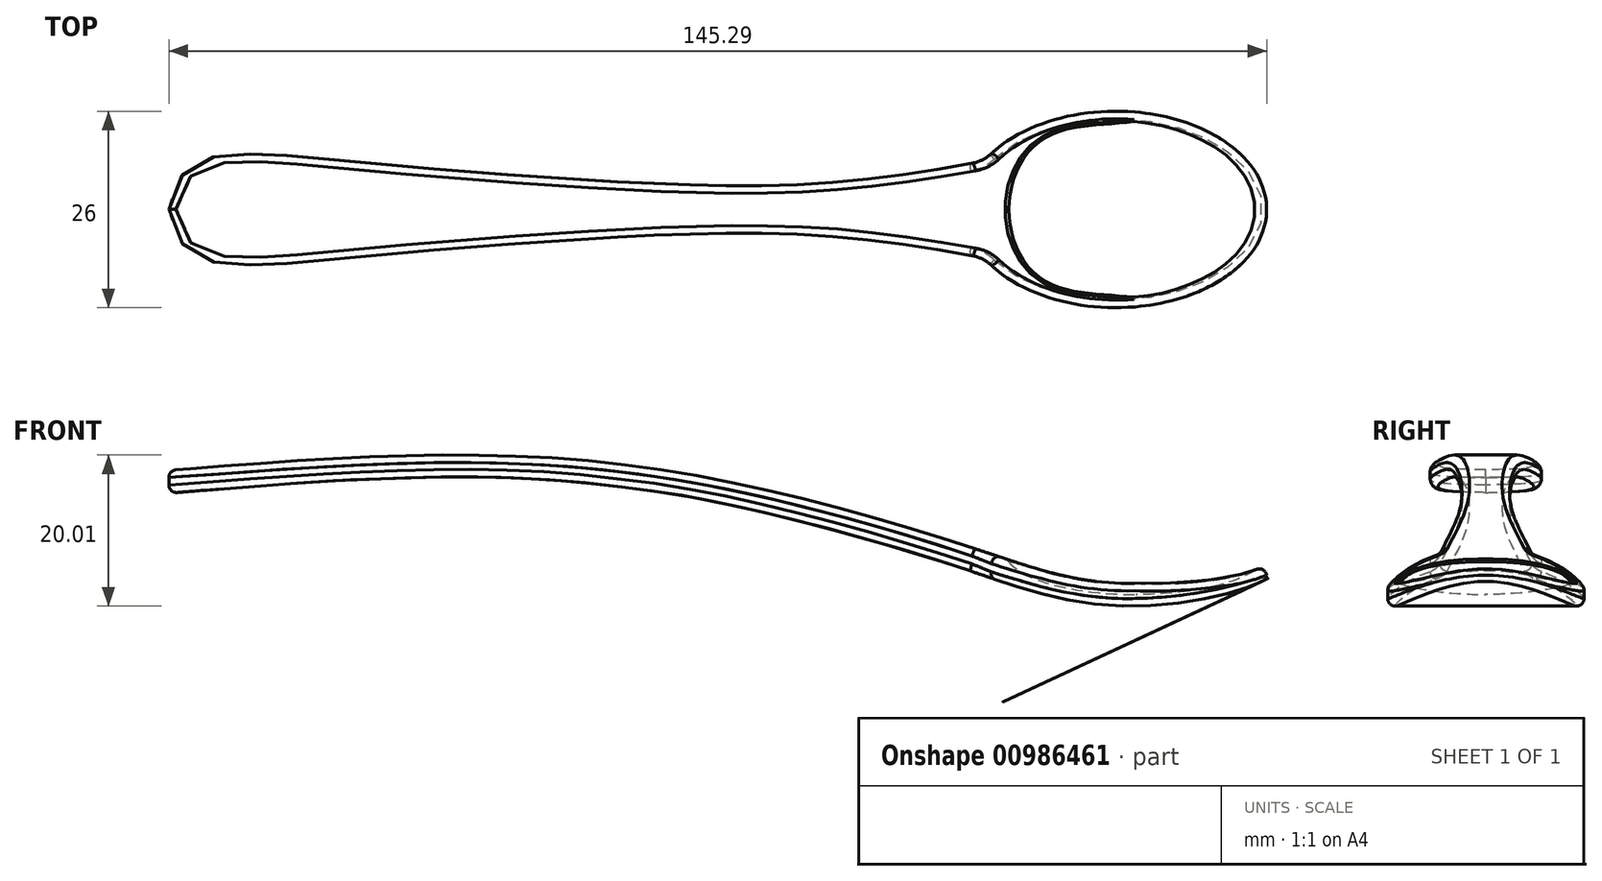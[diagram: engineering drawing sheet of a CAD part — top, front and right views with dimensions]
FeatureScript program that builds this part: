
annotation { "Feature Type Name" : "Feature", "Feature Type Description" : "" }
export const myFeature = defineFeature(function(context is Context, id is Id, definition is map)
    precondition{}
    {
        {
            var Q0;
            Q0=qCreatedBy(makeId("Top.planeOp"),FACE);
            var sketch = newSketch(context, id + "F0", { "sketchPlane" : qUnion([Q0])});
            skEllipticalArc(sketch, "E0", {});
            skFitSpline(sketch, "E1", {"points": [v(-17.42, 6.39) * mm, v(-40.4, 3.38) * mm, v(-73.2, 4.1) * mm, v(-102.87, 6.51) * mm, v(-120.96, 6.51) * mm, v(-124.34, 3.14) * mm, v(-125.3, 0) * mm], "startDerivative": vector(-109.7, -19.22) * mm, "endDerivative": vector(-9.68, -41.52) * mm});
            skLineSegment(sketch, "E2", {"start": v(-125.3, 0) * mm, "end": v(20, 0) * mm, "construction": true});
            skArc(sketch, "E3.filletArc", {"start": v(-19.02, 6.1) * mm, "mid": v(-17.64, 6.56) * mm, "end": v(-16.45, 7.4) * mm});
            skFitSpline(sketch, "E4.MirrorCS", {"points": [v(-17.42, -6.39) * mm, v(-40.4, -3.38) * mm, v(-73.2, -4.1) * mm, v(-102.87, -6.51) * mm, v(-120.96, -6.51) * mm, v(-124.34, -3.14) * mm, v(-125.3, 0) * mm], "startDerivative": vector(-109.7, 19.22) * mm, "endDerivative": vector(-9.68, 41.52) * mm});
            skEllipticalArc(sketch, "E5.MirrorCS", {});
            skArc(sketch, "E6.MirrorCS", {"start": v(-19.02, -6.1) * mm, "mid": v(-17.64, -6.56) * mm, "end": v(-16.45, -7.4) * mm});
            const initialGuessF0  = {"E0": [0, 0, 1, 0, 0.02, 0.013, 0, 2.5369205259482692], "E5.MirrorCS": [0, 0, 1, 0, 0.02, 0.013, 3.746264781231317, 0]};
            skSetInitialGuess(sketch, initialGuessF0);
            skSolve(sketch);
        }
        {
            var Q0;
            Q0=makeQuery(id+"F0.imprint","IMPRINT",FACE,{"disambiguationData":[TD([[makeQuery(id+"F0.imprint","IMPRINT",EDGE,{"derivedFrom":sQuery(id+"F0.wireOp",EDGE,"E0")}),1.0]])]});
            extrude(context, id + "F1", {"entities" : qUnion([Q0]), "depth" : 25 * mm, "offsetDistance" : 25 * mm});
        }
        {
            var Q0;
            Q0=qCreatedBy(makeId("Front.planeOp"),FACE);
            var sketch = newSketch(context, id + "F2", { "sketchPlane" : qUnion([Q0])});
            skLineSegment(sketch, "E7.0", {"start": v(-125.3, 25) * mm, "end": v(-125.3, 19.75) * mm});
            skLineSegment(sketch, "E8", {"start": v(20, 25) * mm, "end": v(20, 8.84) * mm});
            skFitSpline(sketch, "E9", {"points": [v(-125.3, 19.75) * mm, v(-92.2, 21.75) * mm, v(-59.48, 19.75) * mm, v(-29.68, 12.84) * mm, v(-15.87, 8.48) * mm, v(0, 4.85) * mm, v(16.12, 7.03) * mm, v(20, 8.84) * mm], "startDerivative": vector(178.78, 14.39) * mm, "endDerivative": vector(46, 26.97) * mm});
            skFitSpline(sketch, "E10.0", {"points": [v(-125.06, 16.76) * mm, v(-121.34, 17.06) * mm, v(-113.9, 17.66) * mm, v(-102.82, 18.4) * mm, v(-91.86, 18.83) * mm, v(-81.03, 18.8) * mm, v(-72.02, 18.28) * mm, v(-64.75, 17.5) * mm, v(-57.4, 16.44) * mm, v(-49.91, 14.95) * mm, v(-42.74, 13.26) * mm, v(-38.5, 12.18) * mm, v(-35.3, 11.31) * mm, v(-33.01, 10.68) * mm, v(-30.85, 10.06) * mm, v(-28.84, 9.47) * mm, v(-26.96, 8.9) * mm, v(-24.58, 8.18) * mm, v(-21.8, 7.3) * mm, v(-19.1, 6.4) * mm, v(-16.9, 5.67) * mm, v(-15.19, 5.09) * mm, v(-13.4, 4.5) * mm, v(-10.9, 3.73) * mm, v(-8.26, 3.01) * mm, v(-5.46, 2.44) * mm, v(-3.29, 2.1) * mm, v(-1.03, 1.88) * mm, v(1.3, 1.79) * mm, v(3.63, 1.83) * mm, v(6.72, 2.04) * mm, v(10.43, 2.53) * mm, v(14.4, 3.36) * mm, v(17.09, 4.15) * mm, v(18.78, 4.82) * mm, v(19.86, 5.32) * mm, v(20.77, 5.82) * mm, v(21.28, 6.12) * mm, v(21.52, 6.26) * mm]});
            skFitSpline(sketch, "E11.0", {"points": [v(-17.42, 25) * mm, v(-24.68, 25) * mm, v(-40.59, 25) * mm, v(-73.4, 25) * mm, v(-101.07, 25) * mm, v(-121, 25) * mm, v(-124.53, 25) * mm, v(-125.06, 25) * mm, v(-125.3, 25) * mm]});
            skLineSegment(sketch, "E12.0", {"start": v(-16.45, 25) * mm, "end": v(20, 25) * mm});
            skPoint(sketch, "E13.0", {"position": v(-17.64, 25) * mm});
            skLineSegment(sketch, "E14", {"start": v(-125.3, 25) * mm, "end": v(20, 25) * mm});
            skLineSegment(sketch, "E15.trimOffspring", {"start": v(20, 5.4) * mm, "end": v(20, 0) * mm});
            skLineSegment(sketch, "E16", {"start": v(-125.06, 16.76) * mm, "end": v(-125.3, 16.74) * mm});
            skLineSegment(sketch, "E17", {"start": v(-125.3, 16.74) * mm, "end": v(-125.3, 0) * mm});
            skPoint(sketch, "E18.orphan", {"position": v(-125.54, 16.72) * mm});
            skLineSegment(sketch, "E19", {"start": v(-125.3, 0) * mm, "end": v(20, 0) * mm});
            skSolve(sketch);
        }
        {
            var Q0;
            Q0 = qSketchRegion(id + "F2", true);
            extrude(context, id + "F3", {"entities" : qUnion([Q0]), "operationType" : NewBodyOperationType.REMOVE, "endBound" : BoundingType.THROUGH_ALL, "oppositeDirection" : true, "depth" : 25 * mm, "offsetDistance" : 25 * mm, "hasSecondDirection" : true, "secondDirectionBound" : SecondDirectionBoundingType.THROUGH_ALL, "secondDirectionOppositeDirection" : false, "secondDirectionDepth" : 25 * mm});
        }
        {
            var Q0;
            Q0=qCreatedBy(makeId("Front.planeOp"),FACE);
            var sketch = newSketch(context, id + "F4", { "sketchPlane" : qUnion([Q0])});
            skEllipticalArc(sketch, "E20", {});
            skLineSegment(sketch, "E21", {"start": v(2.75, 14.47) * mm, "end": v(2.75, 3.33) * mm});
            const initialGuessF4  = {"E20": [0.002752911997959018, 0.00890183262526989, 1, 0, 0.017286780356269477, 0.005572034292418175, 1.5707963267948966, 4.71238898038469]};
            skSetInitialGuess(sketch, initialGuessF4);
            skSolve(sketch);
        }
        {
            var Q0;
            Q0 = qSketchRegion(id + "F4", true);
            var Q1;
            Q1=sQuery(id+"F4.wireOp",EDGE,"E21");
            revolve(context, id + "F5", {"operationType" : NewBodyOperationType.REMOVE, "surfaceOperationType" : NewSurfaceOperationType.NEW, "entities" : qUnion([Q0]), "axis" : qUnion([Q1]), "revolveType" : RevolveType.FULL, "oppositeDirection" : true});
        }
        {
            var Q0;
            Q0=makeQuery(id+"F3.boolean.opBoolean","INTERSECT",EDGE,{"derivedFrom":[makeQuery(id+"F1.opExtrude","SWEPT_FACE",FACE,{"disambiguationData":[OSD([sQuery(id+"F0.wireOp",EDGE,"E4.MirrorCS")])]}),makeQuery(id+"F3.opExtrude","SWEPT_FACE",FACE,{"disambiguationData":[OSD([sQuery(id+"F2.wireOp",EDGE,"E9")])]})]});
            var Q1;
            Q1=makeQuery(id+"F3.boolean.opBoolean","INTERSECT",EDGE,{"derivedFrom":[makeQuery(id+"F1.opExtrude","SWEPT_FACE",FACE,{"disambiguationData":[OSD([sQuery(id+"F0.wireOp",EDGE,"E1")])]}),makeQuery(id+"F3.opExtrude","SWEPT_FACE",FACE,{"disambiguationData":[OSD([sQuery(id+"F2.wireOp",EDGE,"E9")])]})]});
            var Q2;
            Q2=makeQuery(id+"F3.boolean.opBoolean","INTERSECT",EDGE,{"derivedFrom":[makeQuery(id+"F1.opExtrude","SWEPT_FACE",FACE,{"disambiguationData":[OSD([sQuery(id+"F0.wireOp",EDGE,"E4.MirrorCS")])]}),makeQuery(id+"F3.opExtrude","SWEPT_FACE",FACE,{"disambiguationData":[OSD([sQuery(id+"F2.wireOp",EDGE,"E10.0")])]})]});
            var Q3;
            Q3=makeQuery(id+"F3.boolean.opBoolean","INTERSECT",EDGE,{"derivedFrom":[makeQuery(id+"F1.opExtrude","SWEPT_FACE",FACE,{"disambiguationData":[OSD([sQuery(id+"F0.wireOp",EDGE,"E0"),sQuery(id+"F0.wireOp",EDGE,"E5.MirrorCS")])]}),makeQuery(id+"F3.opExtrude","SWEPT_FACE",FACE,{"disambiguationData":[OSD([sQuery(id+"F2.wireOp",EDGE,"E10.0")])]})]});
            var Q4;
            Q4=makeQuery(id+"F3.boolean.opBoolean","INTERSECT",EDGE,{"derivedFrom":[makeQuery(id+"F1.opExtrude","SWEPT_FACE",FACE,{"disambiguationData":[OSD([sQuery(id+"F0.wireOp",EDGE,"E6.MirrorCS")])]}),makeQuery(id+"F3.opExtrude","SWEPT_FACE",FACE,{"disambiguationData":[OSD([sQuery(id+"F2.wireOp",EDGE,"E9")])]})]});
            var Q5;
            {var subQ0=makeQuery(id+"F1.opExtrude","SWEPT_FACE",FACE,{"disambiguationData":[OSD([sQuery(id+"F0.wireOp",EDGE,"E0"),sQuery(id+"F0.wireOp",EDGE,"E5.MirrorCS")])]});var subQ1=makeQuery(id+"F3.opExtrude","SWEPT_FACE",FACE,{"disambiguationData":[OSD([sQuery(id+"F2.wireOp",EDGE,"E9")])]});Q5=makeQuery(id+"F5.boolean.opBoolean","SPLIT",EDGE,{"disambiguationData":[TD([makeQuery(id+"F1.opExtrude","SWEPT_FACE",FACE,{"disambiguationData":[OSD([sQuery(id+"F0.wireOp",EDGE,"E6.MirrorCS")])]})])],"derivedFrom":makeQuery(id+"F3.boolean.opBoolean","INTERSECT",EDGE,{"derivedFrom":[subQ0,subQ1]})});}
            var Q6;
            Q6=makeQuery(id+"F3.boolean.opBoolean","INTERSECT",EDGE,{"derivedFrom":[makeQuery(id+"F1.opExtrude","SWEPT_FACE",FACE,{"disambiguationData":[OSD([sQuery(id+"F0.wireOp",EDGE,"E6.MirrorCS")])]}),makeQuery(id+"F3.opExtrude","SWEPT_FACE",FACE,{"disambiguationData":[OSD([sQuery(id+"F2.wireOp",EDGE,"E10.0")])]})]});
            var Q7;
            Q7=makeQuery(id+"F3.boolean.opBoolean","INTERSECT",EDGE,{"derivedFrom":[makeQuery(id+"F1.opExtrude","SWEPT_FACE",FACE,{"disambiguationData":[OSD([sQuery(id+"F0.wireOp",EDGE,"E3.filletArc")])]}),makeQuery(id+"F3.opExtrude","SWEPT_FACE",FACE,{"disambiguationData":[OSD([sQuery(id+"F2.wireOp",EDGE,"E9")])]})]});
            var Q8;
            Q8=makeQuery(id+"F5.boolean.opBoolean","INTERSECT",EDGE,{"derivedFrom":[makeQuery(id+"F1.opExtrude","SWEPT_FACE",FACE,{"disambiguationData":[OSD([sQuery(id+"F0.wireOp",EDGE,"E0"),sQuery(id+"F0.wireOp",EDGE,"E5.MirrorCS")])]}),makeQuery(id+"F5.opRevolve","SWEPT_FACE",FACE,{"disambiguationData":[OSD([sQuery(id+"F4.wireOp",EDGE,"E20")])]})]});
            var Q9;
            Q9=makeQuery(id+"F5.boolean.opBoolean","INTERSECT",EDGE,{"derivedFrom":[makeQuery(id+"F3.boolean.opBoolean","COPY",FACE,{"derivedFrom":makeQuery(id+"F3.opExtrude","SWEPT_FACE",FACE,{"disambiguationData":[OSD([sQuery(id+"F2.wireOp",EDGE,"E9")])]})}),makeQuery(id+"F5.opRevolve","SWEPT_FACE",FACE,{"disambiguationData":[OSD([sQuery(id+"F4.wireOp",EDGE,"E20")])]})]});
            var Q10;
            Q10=makeQuery(id+"F3.boolean.opBoolean","INTERSECT",EDGE,{"derivedFrom":[makeQuery(id+"F1.opExtrude","SWEPT_FACE",FACE,{"disambiguationData":[OSD([sQuery(id+"F0.wireOp",EDGE,"E3.filletArc")])]}),makeQuery(id+"F3.opExtrude","SWEPT_FACE",FACE,{"disambiguationData":[OSD([sQuery(id+"F2.wireOp",EDGE,"E10.0")])]})]});
            var Q11;
            Q11=makeQuery(id+"F3.boolean.opBoolean","INTERSECT",EDGE,{"derivedFrom":[makeQuery(id+"F1.opExtrude","SWEPT_FACE",FACE,{"disambiguationData":[OSD([sQuery(id+"F0.wireOp",EDGE,"E1")])]}),makeQuery(id+"F3.opExtrude","SWEPT_FACE",FACE,{"disambiguationData":[OSD([sQuery(id+"F2.wireOp",EDGE,"E10.0")])]})]});
            var Q12;
            Q12=makeQuery(id+"F3.boolean.opBoolean","COPY",EDGE,{"derivedFrom":makeQuery(id+"F3.opExtrude","SWEPT_EDGE",EDGE,{"disambiguationData":[OSD([sQuery(id+"F2.wireOp",EDGE,"E10.0"),sQuery(id+"F2.wireOp",EDGE,"E16")])]})});
            fillet(context, id + "F6", {"entities" : qUnion([Q0, Q1, Q2, Q3, Q4, Q5, Q6, Q7, Q8, Q9, Q10, Q11, Q12]), "radius" : 1 * mm, "tangentPropagation" : true, "allowEdgeOverflow" : false});
        }
    });
